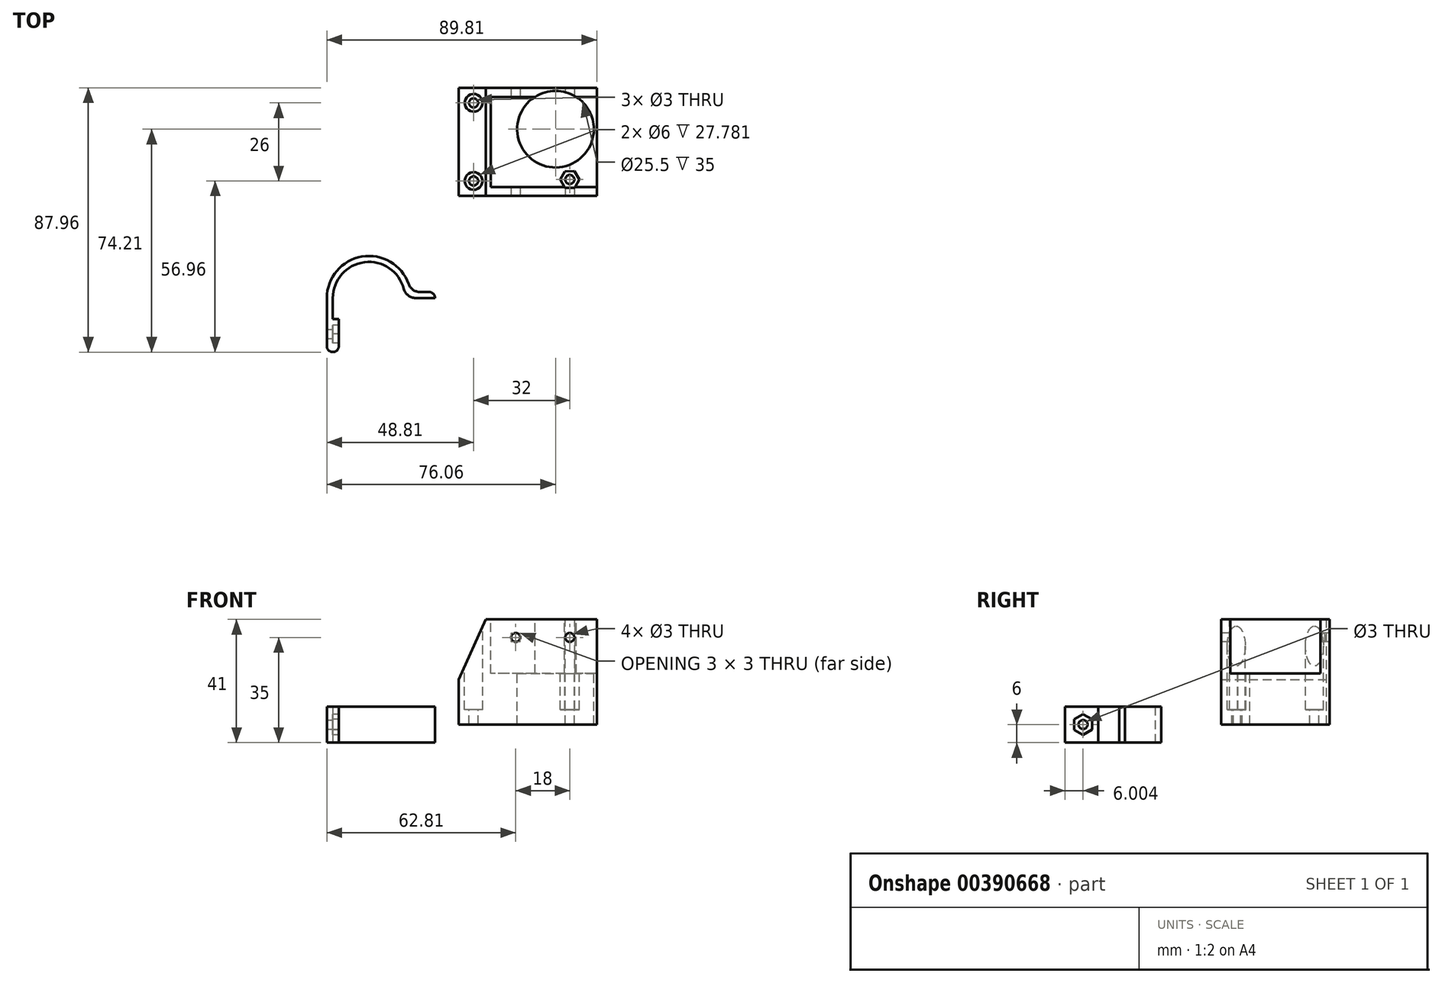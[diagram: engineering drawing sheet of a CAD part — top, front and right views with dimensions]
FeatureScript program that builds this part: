
annotation { "Feature Type Name" : "Feature", "Feature Type Description" : "" }
export const myFeature = defineFeature(function(context is Context, id is Id, definition is map)
    precondition{}
    {
        {
            var Q0;
            Q0=qCreatedBy(makeId("Top.planeOp"),FACE);
            var sketch = newSketch(context, id + "F0", { "sketchPlane" : qUnion([Q0])});
            skLineSegment(sketch, "E0.bottom", {"start": v(23, 18) * mm, "end": v(-23, 18) * mm});
            skLineSegment(sketch, "E0.top", {"start": v(23, -18) * mm, "end": v(-23, -18) * mm});
            skLineSegment(sketch, "E0.left", {"start": v(23, 18) * mm, "end": v(23, -18) * mm});
            skLineSegment(sketch, "E0.right", {"start": v(-23, 18) * mm, "end": v(-23, -18) * mm});
            skPoint(sketch, "E0.middle", {"position": v(0, 0) * mm});
            skSolve(sketch);
        }
        {
            var Q0;
            Q0 = qSketchRegion(id + "F0", true);
            extrude(context, id + "F1", {"entities" : qUnion([Q0]), "depth" : 35 * mm});
        }
        {
            var Q0;
            Q0=makeQuery(id+"F1.opExtrude","CAP_FACE",FACE,{"disambiguationData":[OSD([sQuery(id+"F0.wireOp",EDGE,"E0.bottom"),sQuery(id+"F0.wireOp",EDGE,"E0.top"),sQuery(id+"F0.wireOp",EDGE,"E0.left"),sQuery(id+"F0.wireOp",EDGE,"E0.right")])],"isStart":false});
            var sketch = newSketch(context, id + "F2", { "sketchPlane" : qUnion([Q0])});
            skCircle(sketch, "E1", {"center": v(-18, -13) * mm, "radius": 1.5 * mm});
            skCircle(sketch, "E2", {"center": v(-18, 13) * mm, "radius": 1.5 * mm});
            skCircle(sketch, "E3", {"center": v(14, -12.5) * mm, "radius": 1.5 * mm});
            skCircle(sketch, "E4", {"center": v(-18, 13) * mm, "radius": 3 * mm});
            skCircle(sketch, "E5", {"center": v(-18, -13) * mm, "radius": 3 * mm});
            skCircle(sketch, "E6.cCircle", {"center": v(14, -12.5) * mm, "radius": 3.18 * mm, "construction": true});
            skLineSegment(sketch, "E6.0", {"start": v(12.44, -15.27) * mm, "end": v(10.82, -12.53) * mm});
            skLineSegment(sketch, "E6.1", {"start": v(10.82, -12.53) * mm, "end": v(12.38, -9.77) * mm});
            skLineSegment(sketch, "E6.2", {"start": v(12.38, -9.77) * mm, "end": v(15.56, -9.73) * mm});
            skLineSegment(sketch, "E6.3", {"start": v(15.56, -9.73) * mm, "end": v(17.18, -12.47) * mm});
            skLineSegment(sketch, "E6.4", {"start": v(17.18, -12.47) * mm, "end": v(15.62, -15.23) * mm});
            skLineSegment(sketch, "E6.5", {"start": v(15.62, -15.23) * mm, "end": v(12.44, -15.27) * mm});
            skSolve(sketch);
        }
        {
            var Q0;
            Q0=makeQuery(id+"F2.imprint","IMPRINT",FACE,{"disambiguationData":[TD([[makeQuery(id+"F2.imprint","IMPRINT",EDGE,{"derivedFrom":sQuery(id+"F2.wireOp",EDGE,"E2")}),1.0]])]});
            var Q1;
            Q1=makeQuery(id+"F2.imprint","IMPRINT",FACE,{"disambiguationData":[TD([[makeQuery(id+"F2.imprint","IMPRINT",EDGE,{"derivedFrom":sQuery(id+"F2.wireOp",EDGE,"E1")}),1.0]])]});
            var Q2;
            Q2=makeQuery(id+"F2.imprint","IMPRINT",FACE,{"disambiguationData":[TD([[makeQuery(id+"F2.imprint","IMPRINT",EDGE,{"derivedFrom":sQuery(id+"F2.wireOp",EDGE,"E3")}),1.0]])]});
            extrude(context, id + "F3", {"entities" : qUnion([Q0, Q1, Q2]), "operationType" : NewBodyOperationType.REMOVE, "oppositeDirection" : true, "depth" : 50 * mm});
        }
        {
            var Q0;
            Q0 = qSketchRegion(id + "F2", true);
            extrude(context, id + "F4", {"entities" : qUnion([Q0]), "operationType" : NewBodyOperationType.REMOVE, "oppositeDirection" : true, "depth" : 30 * mm});
        }
        {
            var Q0;
            Q0=makeQuery(id+"F1.opExtrude","CAP_FACE",FACE,{"disambiguationData":[OSD([sQuery(id+"F0.wireOp",EDGE,"E0.bottom"),sQuery(id+"F0.wireOp",EDGE,"E0.top"),sQuery(id+"F0.wireOp",EDGE,"E0.left"),sQuery(id+"F0.wireOp",EDGE,"E0.right")])],"isStart":false});
            var sketch = newSketch(context, id + "F5", { "sketchPlane" : qUnion([Q0])});
            skLineSegment(sketch, "E7.bottom", {"start": v(23, -15) * mm, "end": v(-12.25, -15) * mm});
            skLineSegment(sketch, "E7.top", {"start": v(23, 15) * mm, "end": v(-12.25, 15) * mm});
            skLineSegment(sketch, "E7.left", {"start": v(23, -15) * mm, "end": v(23, 15) * mm});
            skLineSegment(sketch, "E7.right", {"start": v(-12.25, -15) * mm, "end": v(-12.25, 15) * mm});
            skSolve(sketch);
        }
        {
            var Q0;
            Q0=makeQuery(id+"F5.imprint","IMPRINT",FACE,{"disambiguationData":[TD([[makeQuery(id+"F5.imprint","IMPRINT",EDGE,{"derivedFrom":sQuery(id+"F5.wireOp",EDGE,"E7.bottom")}),-1.0]])]});
            extrude(context, id + "F6", {"entities" : qUnion([Q0]), "operationType" : NewBodyOperationType.REMOVE, "oppositeDirection" : true, "depth" : 18 * mm});
        }
        {
            var Q0;
            Q0=makeQuery(id+"F6.boolean.opBoolean","COPY",FACE,{"derivedFrom":makeQuery(id+"F6.opExtrude","CAP_FACE",FACE,{"disambiguationData":[OSD([sQuery(id+"F5.wireOp",EDGE,"E7.bottom"),sQuery(id+"F5.wireOp",EDGE,"E7.top"),sQuery(id+"F5.wireOp",EDGE,"E7.left"),sQuery(id+"F5.wireOp",EDGE,"E7.right")])],"isStart":false})});
            var sketch = newSketch(context, id + "F7", { "sketchPlane" : qUnion([Q0])});
            skCircle(sketch, "E8", {"center": v(9.25, 4.25) * mm, "radius": 12.75 * mm});
            skLineSegment(sketch, "E9", {"start": v(9.25, 4.25) * mm, "end": v(22, 4.25) * mm, "construction": true});
            skLineSegment(sketch, "E10", {"start": v(9.25, 4.25) * mm, "end": v(9.25, 17) * mm, "construction": true});
            skSolve(sketch);
        }
        {
            var Q0;
            Q0=makeQuery(id+"F7.imprint","IMPRINT",FACE,{"disambiguationData":[TD([[makeQuery(id+"F7.imprint","IMPRINT",EDGE,{"derivedFrom":sQuery(id+"F7.wireOp",EDGE,"E8")}),1.0]])]});
            extrude(context, id + "F8", {"entities" : qUnion([Q0]), "operationType" : NewBodyOperationType.REMOVE, "oppositeDirection" : true, "depth" : 50 * mm, "symmetric" : true});
        }
        {
            var Q0;
            Q0=makeQuery(id+"F6.boolean.opBoolean","COPY",FACE,{"derivedFrom":makeQuery(id+"F6.opExtrude","SWEPT_FACE",FACE,{"disambiguationData":[OSD([sQuery(id+"F5.wireOp",EDGE,"E7.top")])]})});
            var sketch = newSketch(context, id + "F9", { "sketchPlane" : qUnion([Q0])});
            skCircle(sketch, "E11", {"center": v(14, 29) * mm, "radius": 1.5 * mm});
            skCircle(sketch, "E12", {"center": v(-4, 29) * mm, "radius": 1.5 * mm});
            skSolve(sketch);
        }
        {
            var Q0;
            Q0 = qSketchRegion(id + "F9", true);
            extrude(context, id + "F10", {"entities" : qUnion([Q0]), "operationType" : NewBodyOperationType.REMOVE, "oppositeDirection" : true, "depth" : 100 * mm, "symmetric" : true});
        }
        {
            var Q0;
            Q0=makeQuery(id+"F1.opExtrude","CAP_EDGE",EDGE,{"disambiguationData":[OSD([sQuery(id+"F0.wireOp",EDGE,"E0.right")])],"isStart":false});
            chamfer(context, id + "F11", {"entities" : qUnion([Q0]), "chamferType" : ChamferType.TWO_OFFSETS, "width1" : 9 * mm, "oppositeDirection" : false, "width2" : 20 * mm, "tangentPropagation" : true});
        }
        {
            var Q0;
            Q0=qCreatedBy(makeId("Top.planeOp"),FACE);
            var sketch = newSketch(context, id + "F12", { "sketchPlane" : qUnion([Q0])});
            skCircle(sketch, "E13", {"center": v(-52.8, -51.96) * mm, "radius": 12 * mm});
            skCircle(sketch, "E14.0", {"center": v(-52.8, -51.96) * mm, "radius": 14 * mm});
            skLineSegment(sketch, "E15", {"start": v(-66.8, -51.96) * mm, "end": v(-38.8, -51.96) * mm, "construction": true});
            skLineSegment(sketch, "E16.bottom", {"start": v(-66.8, -51.96) * mm, "end": v(-64.8, -51.96) * mm});
            skLineSegment(sketch, "E16.top", {"start": v(-66.8, -69.96) * mm, "end": v(-64.8, -69.96) * mm});
            skLineSegment(sketch, "E16.left", {"start": v(-66.8, -51.96) * mm, "end": v(-66.8, -69.96) * mm});
            skLineSegment(sketch, "E16.right", {"start": v(-64.8, -51.96) * mm, "end": v(-64.8, -69.96) * mm});
            skLineSegment(sketch, "E17.bottom", {"start": v(-40.8, -51.96) * mm, "end": v(-30.8, -51.96) * mm});
            skLineSegment(sketch, "E17.top", {"start": v(-40.8, -49.96) * mm, "end": v(-30.8, -49.96) * mm});
            skLineSegment(sketch, "E17.left", {"start": v(-40.8, -51.96) * mm, "end": v(-40.8, -49.96) * mm});
            skLineSegment(sketch, "E17.right", {"start": v(-30.8, -51.96) * mm, "end": v(-30.8, -49.96) * mm});
            skSolve(sketch);
        }
        {
            var Q0;
            {var subQ0=sQuery(id+"F12.wireOp",EDGE,"E16.bottom");Q0=makeQuery(id+"F12.imprint","IMPRINT",FACE,{"disambiguationData":[TD([[makeQuery(id+"F12.imprint","IMPRINT",EDGE,{"derivedFrom":subQ0}),1.0]])]});}
            var Q1;
            {var subQ5=sQuery(id+"F12.wireOp",EDGE,"E17.right");Q1=makeQuery(id+"F12.imprint","IMPRINT",FACE,{"disambiguationData":[TD([[makeQuery(id+"F12.imprint","IMPRINT",EDGE,{"derivedFrom":subQ5}),1.0]])]});}
            var Q2;
            {var subQ5=sQuery(id+"F12.wireOp",EDGE,"E17.left");Q2=makeQuery(id+"F12.imprint","IMPRINT",FACE,{"disambiguationData":[TD([[makeQuery(id+"F12.imprint","IMPRINT",EDGE,{"derivedFrom":subQ5}),-1.0]])]});}
            var Q3;
            {var subQ0=sQuery(id+"F12.wireOp",EDGE,"E16.bottom");Q3=makeQuery(id+"F12.imprint","IMPRINT",FACE,{"disambiguationData":[TD([[makeQuery(id+"F12.imprint","IMPRINT",EDGE,{"derivedFrom":subQ0}),-1.0]])]});}
            var Q4;
            {var subQ4=sQuery(id+"F12.wireOp",EDGE,"E16.top");Q4=makeQuery(id+"F12.imprint","IMPRINT",FACE,{"disambiguationData":[TD([[makeQuery(id+"F12.imprint","IMPRINT",EDGE,{"derivedFrom":subQ4}),1.0]])]});}
            extrude(context, id + "F13", {"entities" : qUnion([Q0, Q1, Q2, Q3, Q4]), "depth" : 12 * mm, "symmetric" : true});
        }
        {
            var Q0;
            Q0=makeQuery(id+"F13.opExtrude","SWEPT_FACE",FACE,{"disambiguationData":[OSD([sQuery(id+"F12.wireOp",EDGE,"E16.right")])]});
            var sketch = newSketch(context, id + "F14", { "sketchPlane" : qUnion([Q0])});
            skCircle(sketch, "E18", {"center": v(-63.96, 0) * mm, "radius": 1.5 * mm});
            skCircle(sketch, "E19.cCircle", {"center": v(-63.96, 0) * mm, "radius": 3 * mm, "construction": true});
            skLineSegment(sketch, "E19.0", {"start": v(-60.95, -1.72) * mm, "end": v(-63.94, -3.46) * mm});
            skLineSegment(sketch, "E19.1", {"start": v(-63.94, -3.46) * mm, "end": v(-66.95, -1.74) * mm});
            skLineSegment(sketch, "E19.2", {"start": v(-66.95, -1.74) * mm, "end": v(-66.96, 1.72) * mm});
            skLineSegment(sketch, "E19.3", {"start": v(-66.96, 1.72) * mm, "end": v(-63.97, 3.46) * mm});
            skLineSegment(sketch, "E19.4", {"start": v(-63.97, 3.46) * mm, "end": v(-60.96, 1.74) * mm});
            skLineSegment(sketch, "E19.5", {"start": v(-60.96, 1.74) * mm, "end": v(-60.95, -1.72) * mm});
            skPoint(sketch, "E19.0.midPoint", {"position": v(-62.45, -2.6) * mm});
            skLineSegment(sketch, "E20.bottom", {"start": v(-69.96, 6) * mm, "end": v(-58.96, 6) * mm});
            skLineSegment(sketch, "E20.top", {"start": v(-69.96, -6) * mm, "end": v(-58.96, -6) * mm});
            skLineSegment(sketch, "E20.left", {"start": v(-69.96, 6) * mm, "end": v(-69.96, -6) * mm});
            skLineSegment(sketch, "E20.right", {"start": v(-58.96, 6) * mm, "end": v(-58.96, -6) * mm});
            skSolve(sketch);
        }
        {
            var Q0;
            Q0=makeQuery(id+"F14.imprint","IMPRINT",FACE,{"disambiguationData":[TD([[makeQuery(id+"F14.imprint","IMPRINT",EDGE,{"derivedFrom":sQuery(id+"F14.wireOp",EDGE,"E19.0")}),1.0]])]});
            extrude(context, id + "F15", {"entities" : qUnion([Q0]), "operationType" : NewBodyOperationType.ADD, "depth" : 2 * mm});
        }
        {
            var Q0;
            Q0=makeQuery(id+"F14.imprint","IMPRINT",FACE,{"disambiguationData":[TD([[makeQuery(id+"F14.imprint","IMPRINT",EDGE,{"derivedFrom":sQuery(id+"F14.wireOp",EDGE,"E18")}),1.0]])]});
            extrude(context, id + "F16", {"entities" : qUnion([Q0]), "operationType" : NewBodyOperationType.REMOVE, "oppositeDirection" : true, "depth" : 25 * mm});
        }
        {
            var Q0;
            Q0=makeQuery(id+"F13.opExtrude","SWEPT_EDGE",EDGE,{"disambiguationData":[OSD([sQuery(id+"F12.wireOp",EDGE,"24572770-fc28-49ad-a867-e9377c0cc3fc.0"),sQuery(id+"F12.wireOp",EDGE,"QOivRtii-jhSI-htB5-c9gD-8GXYlo5f67iU.top")])]});
            var Q1;
            Q1=makeQuery(id+"F13.opExtrude","SWEPT_EDGE",EDGE,{"disambiguationData":[OSD([sQuery(id+"F12.wireOp",EDGE,"E14.0"),sQuery(id+"F12.wireOp",EDGE,"E17.top")])]});
            var Q2;
            Q2=makeQuery(id+"F15.opExtrude","CAP_EDGE",EDGE,{"disambiguationData":[OSD([sQuery(id+"F14.wireOp",EDGE,"E20.right")])],"isStart":true});
            var Q3;
            Q3=makeQuery(id+"F13.opExtrude","SWEPT_EDGE",EDGE,{"disambiguationData":[OSD([sQuery(id+"F12.wireOp",EDGE,"E13"),sQuery(id+"F12.wireOp",EDGE,"E17.bottom"),sQuery(id+"F12.wireOp",EDGE,"E17.left")])]});
            fillet(context, id + "F17", {"entities" : qUnion([Q0, Q1, Q2, Q3]), "radius" : 4 * mm, "tangentPropagation" : true, "allowEdgeOverflow" : false});
        }
        {
            var Q0;
            Q0=makeQuery(id+"F13.opExtrude","SWEPT_EDGE",EDGE,{"disambiguationData":[OSD([sQuery(id+"F12.wireOp",EDGE,"E16.top"),sQuery(id+"F12.wireOp",EDGE,"E16.left")])]});
            var Q1;
            Q1=makeQuery(id+"F15.opExtrude","CAP_EDGE",EDGE,{"disambiguationData":[OSD([sQuery(id+"F14.wireOp",EDGE,"E20.left")])],"isStart":false});
            var Q2;
            Q2=makeQuery(id+"F13.opExtrude","SWEPT_EDGE",EDGE,{"disambiguationData":[OSD([sQuery(id+"F12.wireOp",EDGE,"E17.top"),sQuery(id+"F12.wireOp",EDGE,"E17.right")])]});
            fillet(context, id + "F18", {"entities" : qUnion([Q0, Q1, Q2]), "radius" : 2 * mm, "tangentPropagation" : true, "allowEdgeOverflow" : false});
        }
    });
